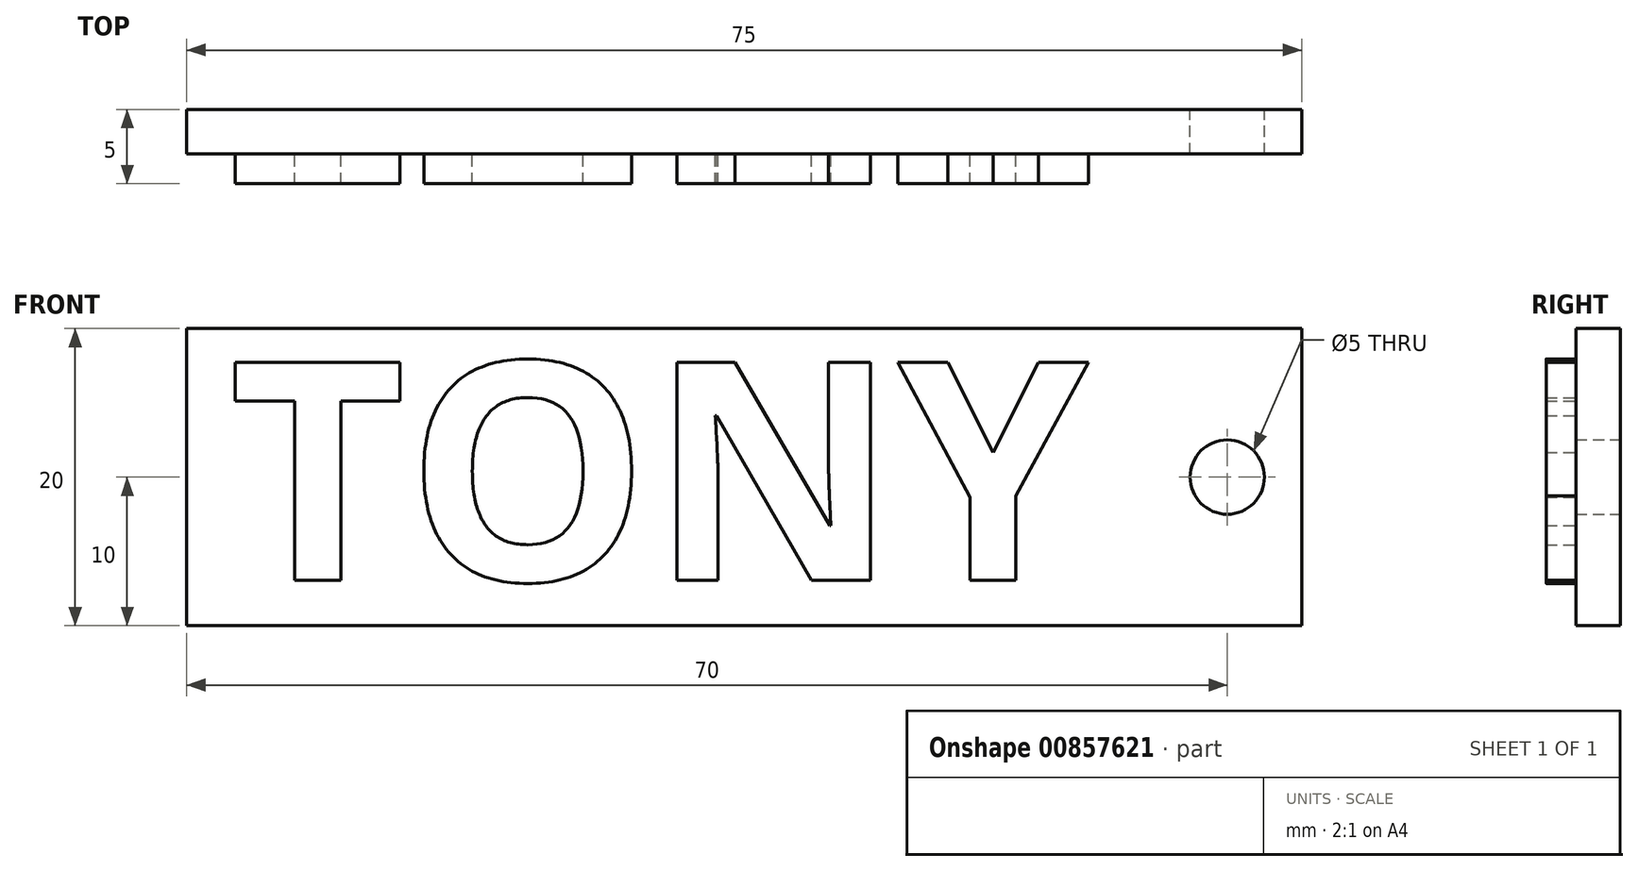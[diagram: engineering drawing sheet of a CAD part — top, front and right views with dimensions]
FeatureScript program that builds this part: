
annotation { "Feature Type Name" : "Feature", "Feature Type Description" : "" }
export const myFeature = defineFeature(function(context is Context, id is Id, definition is map)
    precondition{}
    {
        {
            var Q0;
            Q0=qCreatedBy(makeId("Front.planeOp"),FACE);
            var sketch = newSketch(context, id + "F0", { "sketchPlane" : qUnion([Q0])});
            skLineSegment(sketch, "E0.bottom", {"start": v(0, 0) * mm, "end": v(75, 0) * mm});
            skLineSegment(sketch, "E0.top", {"start": v(0, -20) * mm, "end": v(75, -20) * mm});
            skLineSegment(sketch, "E0.left", {"start": v(0, 0) * mm, "end": v(0, -20) * mm});
            skLineSegment(sketch, "E0.right", {"start": v(75, 0) * mm, "end": v(75, -20) * mm});
            skCircle(sketch, "E1", {"center": v(70, -10) * mm, "radius": 2.5 * mm});
            skSolve(sketch);
        }
        {
            var Q0;
            Q0 = qSketchRegion(id + "F0", true);
            extrude(context, id + "F1", {"entities" : qUnion([Q0]), "depth" : 3 * mm, "offsetDistance" : 25 * mm});
        }
        {
            var Q0;
            Q0=makeQuery(id+"F1.opExtrude","CAP_FACE",FACE,{"disambiguationData":[OSD([sQuery(id+"F0.wireOp",EDGE,"E0.bottom"),sQuery(id+"F0.wireOp",EDGE,"E0.top"),sQuery(id+"F0.wireOp",EDGE,"E0.left"),sQuery(id+"F0.wireOp",EDGE,"E0.right"),sQuery(id+"F0.wireOp",EDGE,"E1")])],"isStart":false});
            var sketch = newSketch(context, id + "F2", { "sketchPlane" : qUnion([Q0])});
            skText(sketch, "E2", { "text": "TONY", "fontName": "OpenSans-Bold.ttf"});
            const initialGuessF2  = {"E2": [0.00285, -0.01696, 1, 0, 0.0148]};
            skSetInitialGuess(sketch, initialGuessF2);
            skSolve(sketch);
        }
        {
            var Q0;
            Q0 = qSketchRegion(id + "F2", true);
            extrude(context, id + "F3", {"entities" : qUnion([Q0]), "operationType" : NewBodyOperationType.ADD, "depth" : 2 * mm, "offsetDistance" : 25 * mm});
        }
    });
